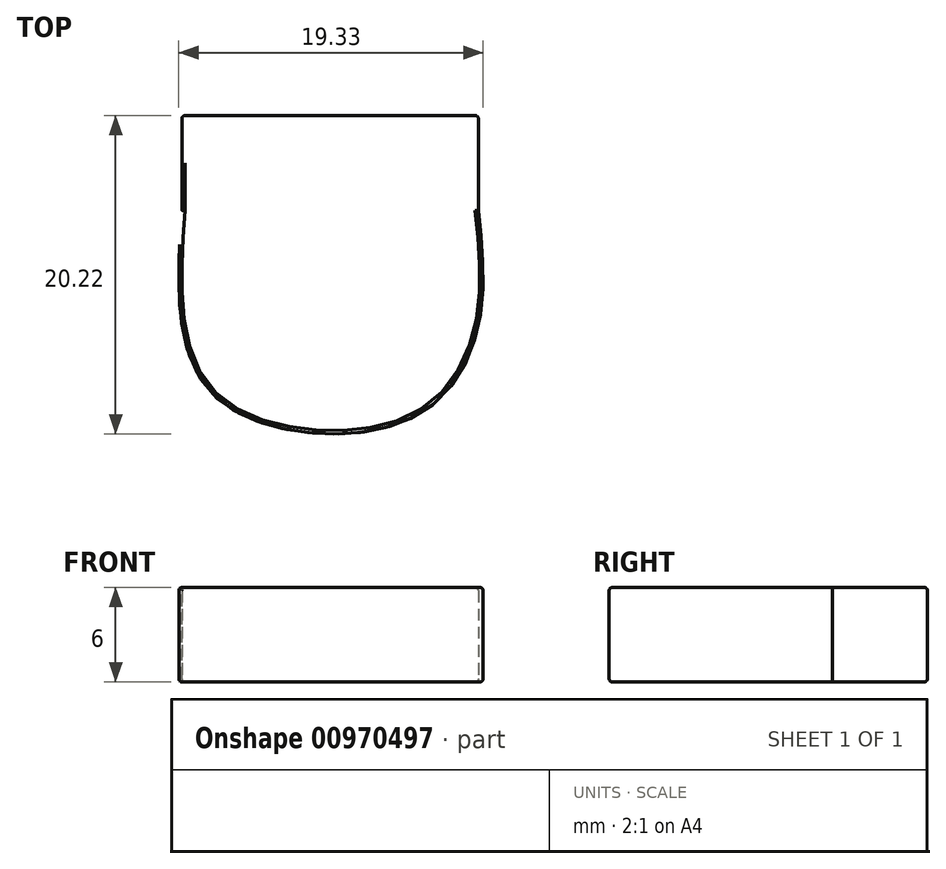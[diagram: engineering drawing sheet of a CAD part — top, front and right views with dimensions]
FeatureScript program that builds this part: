
annotation { "Feature Type Name" : "Feature", "Feature Type Description" : "" }
export const myFeature = defineFeature(function(context is Context, id is Id, definition is map)
    precondition{}
    {
        {
            var Q0;
            Q0=qCreatedBy(makeId("Top.planeOp"),FACE);
            var sketch = newSketch(context, id + "F0", { "sketchPlane" : qUnion([Q0])});
            skFitSpline(sketch, "E0", {"points": [v(11.4, 6.07) * mm, v(11.4, -1.2) * mm, v(7.18, -7.1) * mm, v(-3.21, -7.1) * mm, v(-7.43, -1.21) * mm, v(-7.43, 6.06) * mm, v(-7.43, 6.07) * mm, v(-7.43, 6.07) * mm, v(-7.43, 7.57) * mm, v(-7.43, 9.08) * mm]});
            skFitSpline(sketch, "E1", {"points": [v(-7.43, 9.08) * mm, v(-7.43, 10.54) * mm, v(-7.43, 12.01) * mm, v(-7.43, 12.1) * mm, v(-7.43, 12.1) * mm, v(-7.43, 12.1) * mm]});
            skFitSpline(sketch, "E2", {"points": [v(-7.43, 12.1) * mm, v(-7.43, 12.1) * mm, v(-7.43, 12.1) * mm, v(-7.19, 12.1) * mm, v(11.16, 12.1) * mm, v(11.4, 12.1) * mm, v(11.4, 12.1) * mm, v(11.4, 12.1) * mm]});
            skFitSpline(sketch, "E3", {"points": [v(11.4, 12.1) * mm, v(11.4, 12.1) * mm, v(11.4, 12.1) * mm, v(11.4, 11.94) * mm, v(11.4, 6.22) * mm, v(11.4, 6.07) * mm, v(11.4, 6.07) * mm, v(11.4, 6.07) * mm]});
            skSolve(sketch);
        }
        {
            var Q0;
            Q0=makeQuery(id+"F0.imprint","IMPRINT",FACE,{"disambiguationData":[TD([[makeQuery(id+"F0.imprint","IMPRINT",EDGE,{"derivedFrom":sQuery(id+"F0.wireOp",EDGE,"E0")}),-1.0]])]});
            extrude(context, id + "F1", {"entities" : qUnion([Q0]), "depth" : 6 * mm, "offsetDistance" : 25 * mm});
        }
        {
            var Q0;
            Q0=makeQuery(id+"F1.opExtrude","CAP_FACE",FACE,{"disambiguationData":[OSD([sQuery(id+"F0.wireOp",EDGE,"E0"),sQuery(id+"F0.wireOp",EDGE,"E1"),sQuery(id+"F0.wireOp",EDGE,"E2"),sQuery(id+"F0.wireOp",EDGE,"E3")])],"isStart":false});
            var Q1;
            Q1=makeQuery(id+"F1.opExtrude","CAP_FACE",FACE,{"disambiguationData":[OSD([sQuery(id+"F0.wireOp",EDGE,"E0"),sQuery(id+"F0.wireOp",EDGE,"E1"),sQuery(id+"F0.wireOp",EDGE,"E2"),sQuery(id+"F0.wireOp",EDGE,"E3")])],"isStart":true});
            fillet(context, id + "F2", {"entities" : qUnion([Q0, Q1]), "radius" : 0.2 * mm, "tangentPropagation" : true, "allowEdgeOverflow" : false});
        }
        {
            var Q0;
            Q0=makeQuery(id+"F1.opExtrude","SWEPT_EDGE",EDGE,{"disambiguationData":[OSD([sQuery(id+"F0.wireOp",EDGE,"E2"),sQuery(id+"F0.wireOp",EDGE,"E3")])]});
            var Q1;
            Q1=makeQuery(id+"F1.opExtrude","SWEPT_EDGE",EDGE,{"disambiguationData":[OSD([sQuery(id+"F0.wireOp",EDGE,"E1"),sQuery(id+"F0.wireOp",EDGE,"E2")])]});
            fillet(context, id + "F3", {"entities" : qUnion([Q0, Q1]), "radius" : 0.2 * mm, "tangentPropagation" : true, "allowEdgeOverflow" : false});
        }
    });
